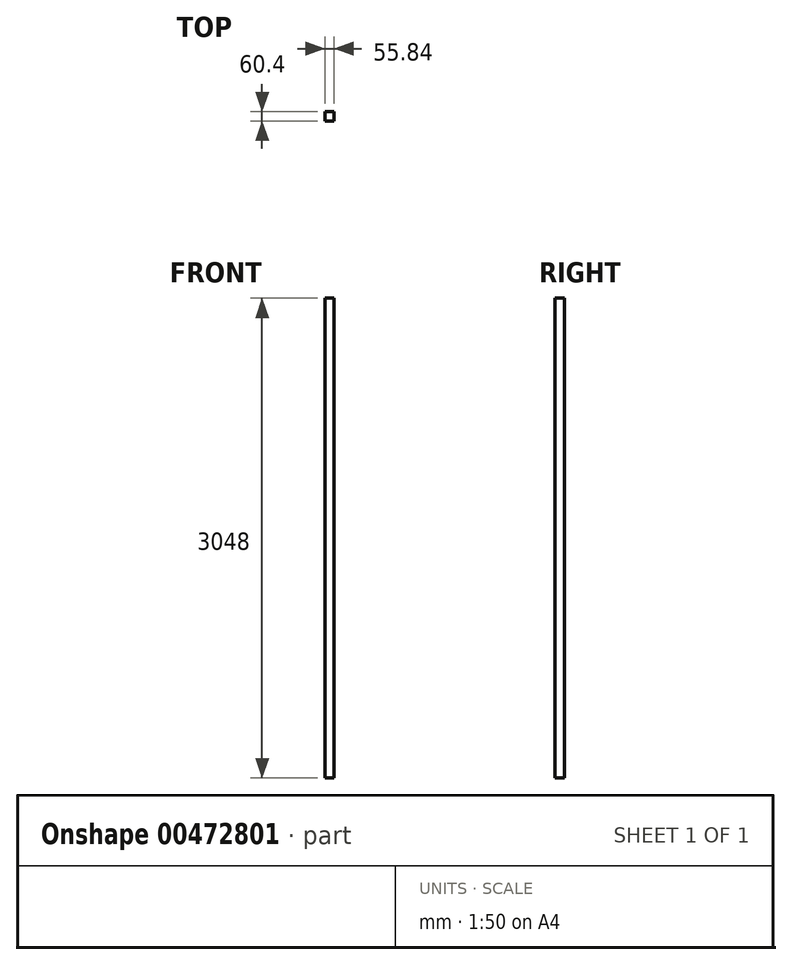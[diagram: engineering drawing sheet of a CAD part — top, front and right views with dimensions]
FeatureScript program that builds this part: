
annotation { "Feature Type Name" : "Feature", "Feature Type Description" : "" }
export const myFeature = defineFeature(function(context is Context, id is Id, definition is map)
    precondition{}
    {
        {
            var Q0;
            Q0=qCreatedBy(makeId("Top.planeOp"),FACE);
            var sketch = newSketch(context, id + "F0", { "sketchPlane" : qUnion([Q0])});
            skLineSegment(sketch, "E0.bottom", {"start": v(-27.92, -30.2) * mm, "end": v(27.92, -30.2) * mm});
            skLineSegment(sketch, "E0.top", {"start": v(-27.92, 30.2) * mm, "end": v(27.92, 30.2) * mm});
            skLineSegment(sketch, "E0.left", {"start": v(-27.92, -30.2) * mm, "end": v(-27.92, 30.2) * mm});
            skLineSegment(sketch, "E0.right", {"start": v(27.92, -30.2) * mm, "end": v(27.92, 30.2) * mm});
            skPoint(sketch, "E0.middle", {"position": v(0, 0) * mm});
            skSolve(sketch);
        }
        {
            var Q0;
            Q0=makeQuery(id+"F0.imprint","IMPRINT",FACE,{"disambiguationData":[TD([[makeQuery(id+"F0.imprint","IMPRINT",EDGE,{"derivedFrom":sQuery(id+"F0.wireOp",EDGE,"E0.bottom")}),1.0]])]});
            extrude(context, id + "F1", {"entities" : qUnion([Q0]), "depth" : 3048 * mm});
        }
    });
